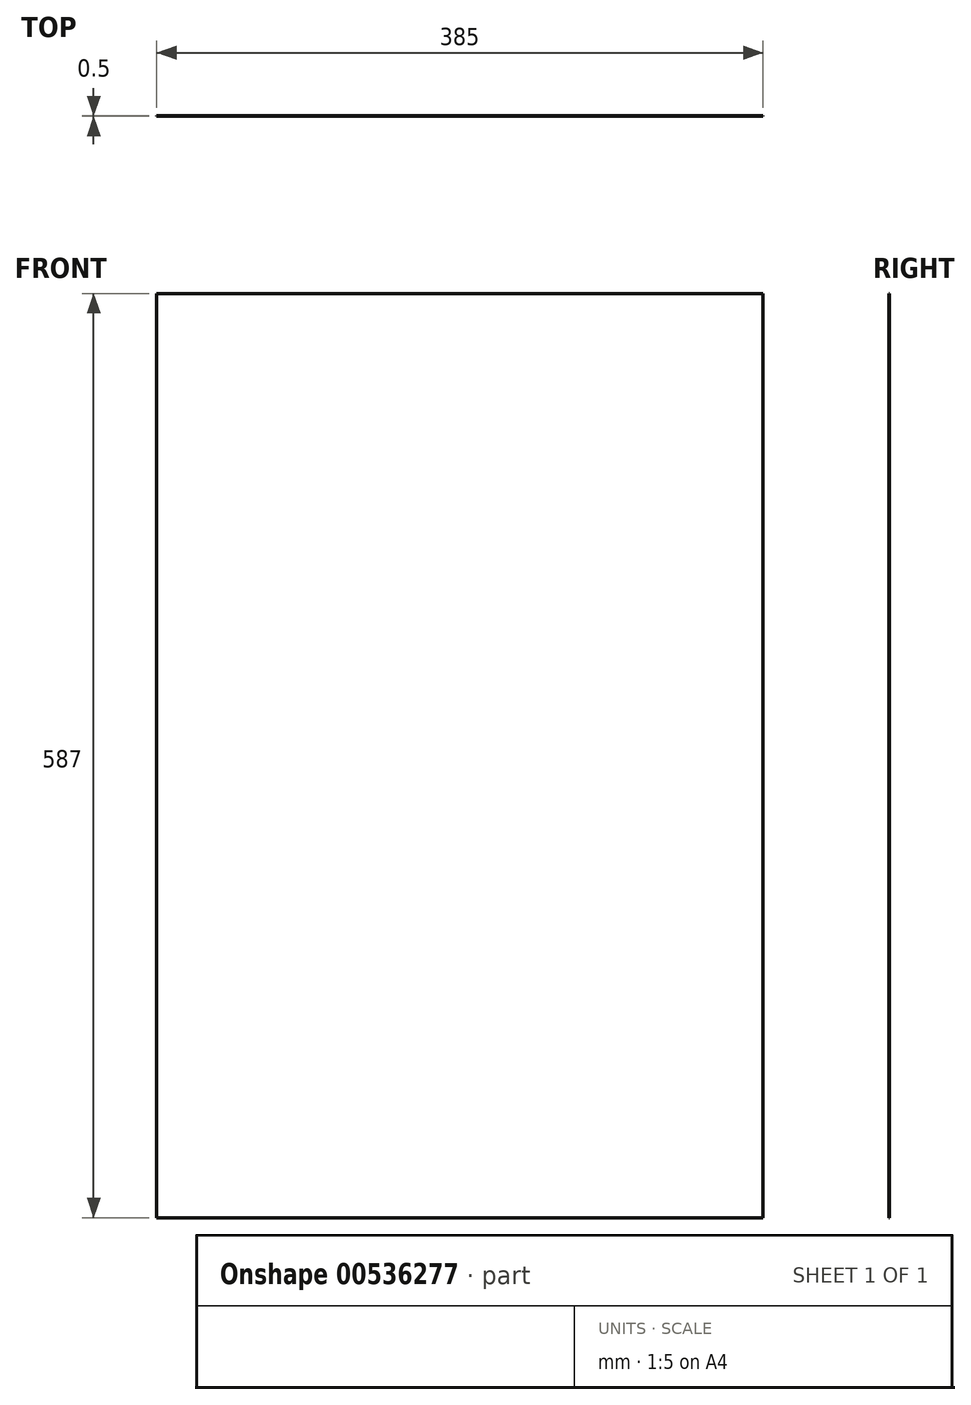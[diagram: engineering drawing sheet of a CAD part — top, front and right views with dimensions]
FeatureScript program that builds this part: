
annotation { "Feature Type Name" : "Feature", "Feature Type Description" : "" }
export const myFeature = defineFeature(function(context is Context, id is Id, definition is map)
    precondition{}
    {
        {
            var Q0;
            Q0=qCreatedBy(makeId("Front.planeOp"),FACE);
            var sketch = newSketch(context, id + "F0", { "sketchPlane" : qUnion([Q0])});
            skLineSegment(sketch, "E0.bottom", {"start": v(-192.5, 293.5) * mm, "end": v(192.5, 293.5) * mm});
            skLineSegment(sketch, "E0.top", {"start": v(-192.5, -293.5) * mm, "end": v(192.5, -293.5) * mm});
            skLineSegment(sketch, "E0.left", {"start": v(-192.5, 293.5) * mm, "end": v(-192.5, -293.5) * mm});
            skLineSegment(sketch, "E0.right", {"start": v(192.5, 293.5) * mm, "end": v(192.5, -293.5) * mm});
            skPoint(sketch, "E0.middle", {"position": v(0, 0) * mm});
            skSolve(sketch);
        }
        {
            var Q0;
            Q0=makeQuery(id+"F0.imprint","IMPRINT",FACE,{"disambiguationData":[TD([[makeQuery(id+"F0.imprint","IMPRINT",EDGE,{"derivedFrom":sQuery(id+"F0.wireOp",EDGE,"E0.bottom")}),-1.0]])]});
            extrude(context, id + "F1", {"entities" : qUnion([Q0]), "depth" : 0.5 * mm, "offsetDistance" : 25 * mm});
        }
    });
